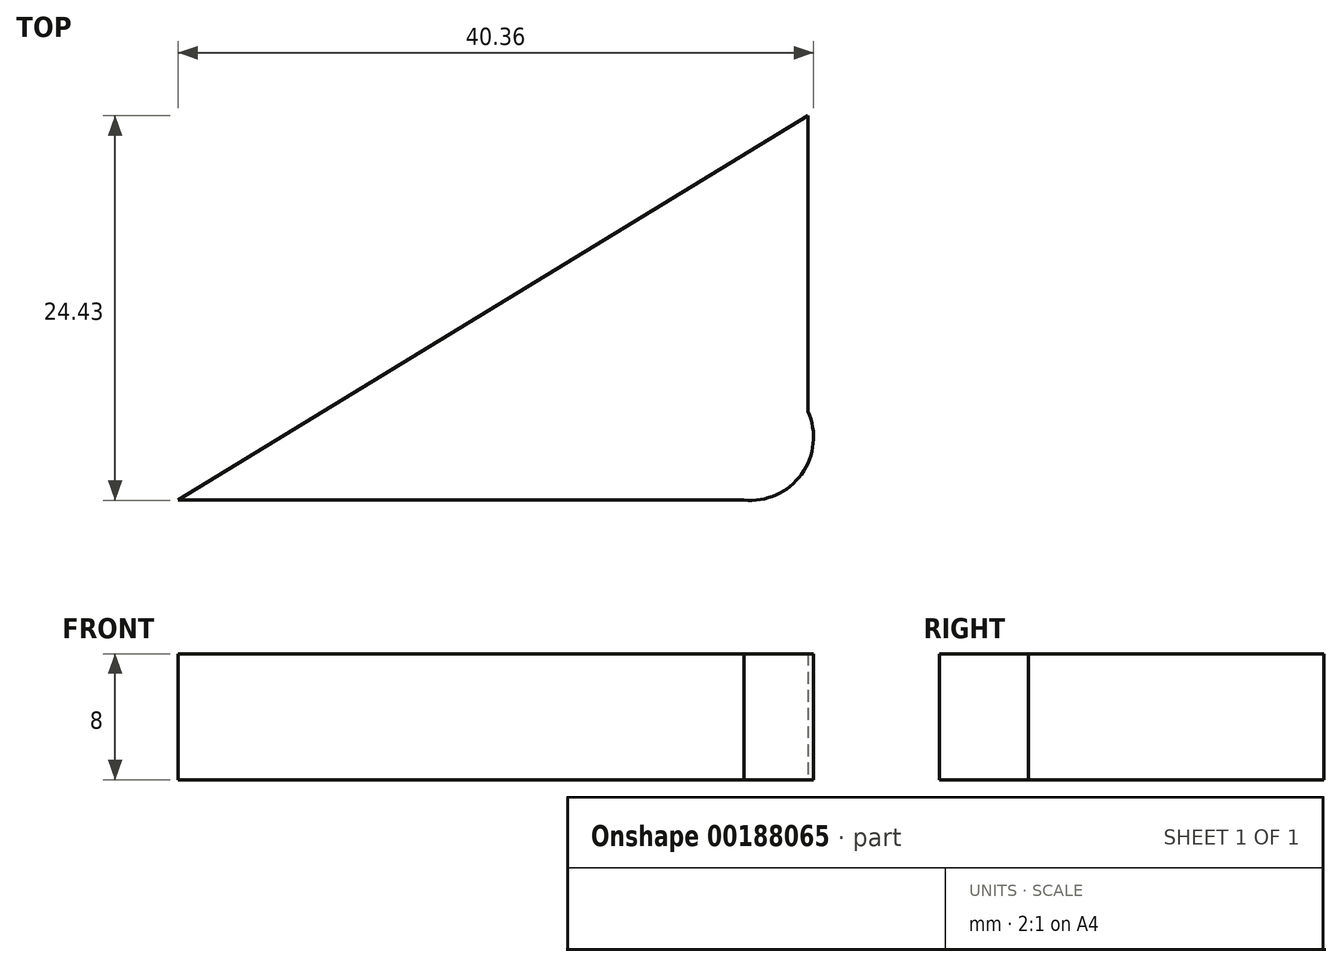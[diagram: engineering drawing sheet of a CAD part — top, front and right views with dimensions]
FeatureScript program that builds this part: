
annotation { "Feature Type Name" : "Feature", "Feature Type Description" : "" }
export const myFeature = defineFeature(function(context is Context, id is Id, definition is map)
    precondition{}
    {
        {
            var Q0;
            Q0=qCreatedBy(makeId("Top.planeOp"),FACE);
            var sketch = newSketch(context, id + "F0", { "sketchPlane" : qUnion([Q0])});
            skArc(sketch, "E0", {"start": v(-22.2, 15.93) * mm, "mid": v(-18.53, 17.56) * mm, "end": v(-18.13, 21.56) * mm});
            skLineSegment(sketch, "E1", {"start": v(-18.13, 21.56) * mm, "end": v(-18.13, 40.33) * mm});
            skLineSegment(sketch, "E2", {"start": v(-18.13, 40.33) * mm, "end": v(-58.13, 15.93) * mm});
            skLineSegment(sketch, "E3", {"start": v(-22.2, 15.93) * mm, "end": v(-58.13, 15.93) * mm});
            skSolve(sketch);
        }
        {
            var Q0;
            Q0=makeQuery(id+"F0.imprint","IMPRINT",FACE,{"disambiguationData":[TD([[makeQuery(id+"F0.imprint","IMPRINT",EDGE,{"derivedFrom":sQuery(id+"F0.wireOp",EDGE,"E0")}),1.0]])]});
            extrude(context, id + "F1", {"entities" : qUnion([Q0]), "depth" : 8 * mm});
        }
    });
